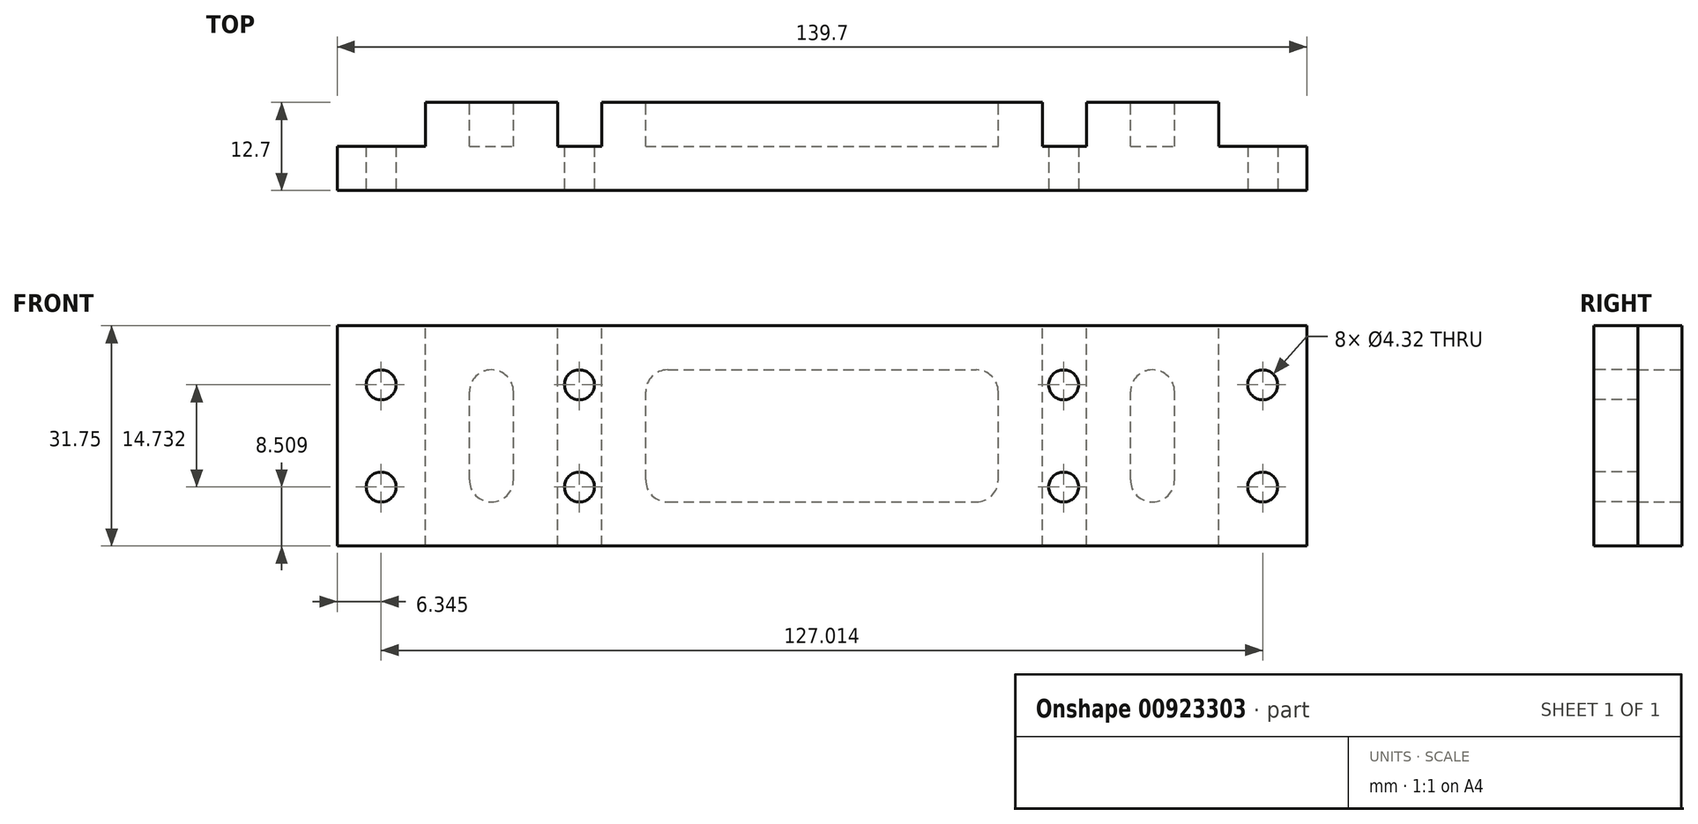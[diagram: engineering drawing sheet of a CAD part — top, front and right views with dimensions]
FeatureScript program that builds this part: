
annotation { "Feature Type Name" : "Feature", "Feature Type Description" : "" }
export const myFeature = defineFeature(function(context is Context, id is Id, definition is map)
    precondition{}
    {
        {
            var Q0;
            Q0=qCreatedBy(makeId("Right.planeOp"),FACE);
            var sketch = newSketch(context, id + "F0", { "sketchPlane" : qUnion([Q0])});
            skLineSegment(sketch, "E0.bottom", {"start": v(0, 0) * mm, "end": v(12.7, 0) * mm});
            skLineSegment(sketch, "E0.top", {"start": v(0, 31.75) * mm, "end": v(12.7, 31.75) * mm});
            skLineSegment(sketch, "E0.left", {"start": v(0, 0) * mm, "end": v(0, 31.75) * mm});
            skLineSegment(sketch, "E0.right", {"start": v(12.7, 0) * mm, "end": v(12.7, 31.75) * mm});
            skSolve(sketch);
        }
        {
            var Q0;
            Q0=makeQuery(id+"F0.imprint","IMPRINT",FACE,{"disambiguationData":[TD([[makeQuery(id+"F0.imprint","IMPRINT",EDGE,{"derivedFrom":sQuery(id+"F0.wireOp",EDGE,"E0.bottom")}),1.0]])]});
            extrude(context, id + "F1", {"entities" : qUnion([Q0]), "depth" : 139.7 * mm, "offsetDistance" : 25.4 * mm});
        }
        {
            var Q0;
            Q0=makeQuery(id+"F1.opExtrude","SWEPT_FACE",FACE,{"disambiguationData":[OSD([sQuery(id+"F0.wireOp",EDGE,"E0.top")])]});
            var sketch = newSketch(context, id + "F2", { "sketchPlane" : qUnion([Q0])});
            skLineSegment(sketch, "E1.bottom", {"start": v(0, 12.7) * mm, "end": v(12.7, 12.7) * mm});
            skLineSegment(sketch, "E1.top", {"start": v(0, 6.35) * mm, "end": v(12.7, 6.35) * mm});
            skLineSegment(sketch, "E1.left", {"start": v(0, 12.7) * mm, "end": v(0, 6.35) * mm});
            skLineSegment(sketch, "E1.right", {"start": v(12.7, 12.7) * mm, "end": v(12.7, 6.35) * mm});
            skLineSegment(sketch, "E2.bottom", {"start": v(139.7, 12.7) * mm, "end": v(127, 12.7) * mm});
            skLineSegment(sketch, "E2.top", {"start": v(139.7, 6.35) * mm, "end": v(127, 6.35) * mm});
            skLineSegment(sketch, "E2.left", {"start": v(139.7, 12.7) * mm, "end": v(139.7, 6.35) * mm});
            skLineSegment(sketch, "E2.right", {"start": v(127, 12.7) * mm, "end": v(127, 6.35) * mm});
            skLineSegment(sketch, "E3.bottom", {"start": v(31.75, 12.7) * mm, "end": v(38.1, 12.7) * mm});
            skLineSegment(sketch, "E3.top", {"start": v(31.75, 6.35) * mm, "end": v(38.1, 6.35) * mm});
            skLineSegment(sketch, "E3.left", {"start": v(31.75, 12.7) * mm, "end": v(31.75, 6.35) * mm});
            skLineSegment(sketch, "E3.right", {"start": v(38.1, 12.7) * mm, "end": v(38.1, 6.35) * mm});
            skLineSegment(sketch, "E4.bottom", {"start": v(101.6, 12.7) * mm, "end": v(107.95, 12.7) * mm});
            skLineSegment(sketch, "E4.top", {"start": v(101.6, 6.35) * mm, "end": v(107.95, 6.35) * mm});
            skLineSegment(sketch, "E4.left", {"start": v(101.6, 12.7) * mm, "end": v(101.6, 6.35) * mm});
            skLineSegment(sketch, "E4.right", {"start": v(107.95, 12.7) * mm, "end": v(107.95, 6.35) * mm});
            skSolve(sketch);
        }
        {
            var Q0;
            Q0=makeQuery(id+"F2.imprint","IMPRINT",FACE,{"disambiguationData":[TD([[makeQuery(id+"F2.imprint","IMPRINT",EDGE,{"derivedFrom":sQuery(id+"F2.wireOp",EDGE,"E1.bottom")}),1.0]])]});
            var Q1;
            Q1=makeQuery(id+"F2.imprint","IMPRINT",FACE,{"disambiguationData":[TD([[makeQuery(id+"F2.imprint","IMPRINT",EDGE,{"derivedFrom":sQuery(id+"F2.wireOp",EDGE,"E3.bottom")}),1.0]])]});
            var Q2;
            Q2=makeQuery(id+"F2.imprint","IMPRINT",FACE,{"disambiguationData":[TD([[makeQuery(id+"F2.imprint","IMPRINT",EDGE,{"derivedFrom":sQuery(id+"F2.wireOp",EDGE,"E4.bottom")}),1.0]])]});
            var Q3;
            Q3=makeQuery(id+"F2.imprint","IMPRINT",FACE,{"disambiguationData":[TD([[makeQuery(id+"F2.imprint","IMPRINT",EDGE,{"derivedFrom":sQuery(id+"F2.wireOp",EDGE,"E2.bottom")}),1.0]])]});
            extrude(context, id + "F3", {"entities" : qUnion([Q0, Q1, Q2, Q3]), "operationType" : NewBodyOperationType.REMOVE, "endBound" : BoundingType.THROUGH_ALL, "oppositeDirection" : true, "depth" : 25.4 * mm, "offsetDistance" : 25.4 * mm});
        }
        {
            var Q0;
            Q0=makeQuery(id+"F1.opExtrude","SWEPT_FACE",FACE,{"disambiguationData":[OSD([sQuery(id+"F0.wireOp",EDGE,"E0.left")])]});
            var sketch = newSketch(context, id + "F4", { "sketchPlane" : qUnion([Q0])});
            skCircle(sketch, "E5", {"center": v(6.34, 23.24) * mm, "radius": 2.16 * mm});
            skCircle(sketch, "E6", {"center": v(6.34, 8.5) * mm, "radius": 2.16 * mm});
            skCircle(sketch, "E7", {"center": v(133.36, 23.24) * mm, "radius": 2.16 * mm});
            skCircle(sketch, "E8", {"center": v(133.36, 8.5) * mm, "radius": 2.16 * mm});
            skLineSegment(sketch, "E9", {"start": v(6.34, 23.24) * mm, "end": v(133.36, 23.24) * mm});
            skLineSegment(sketch, "E10", {"start": v(6.34, 8.5) * mm, "end": v(133.36, 8.5) * mm});
            skSolve(sketch);
        }
        {
            var Q0;
            Q0=makeQuery(id+"F4.imprint","IMPRINT",FACE,{"disambiguationData":[TD([[makeQuery(id+"F4.imprint","IMPRINT",EDGE,{"derivedFrom":sQuery(id+"F4.wireOp",EDGE,"E5")}),1.0]])]});
            var Q1;
            Q1=makeQuery(id+"F4.imprint","IMPRINT",FACE,{"disambiguationData":[TD([[makeQuery(id+"F4.imprint","IMPRINT",EDGE,{"derivedFrom":sQuery(id+"F4.wireOp",EDGE,"E6")}),1.0]])]});
            var Q2;
            Q2=makeQuery(id+"F4.imprint","IMPRINT",FACE,{"disambiguationData":[TD([[makeQuery(id+"F4.imprint","IMPRINT",EDGE,{"derivedFrom":sQuery(id+"F4.wireOp",EDGE,"E8")}),1.0]])]});
            var Q3;
            Q3=makeQuery(id+"F4.imprint","IMPRINT",FACE,{"disambiguationData":[TD([[makeQuery(id+"F4.imprint","IMPRINT",EDGE,{"derivedFrom":sQuery(id+"F4.wireOp",EDGE,"E7")}),1.0]])]});
            var Q4;
            Q4=sQuery(id+"F4.wireOp",EDGE,"E8");
            var Q5;
            Q5=sQuery(id+"F4.wireOp",EDGE,"E7");
            var Q6;
            Q6=sQuery(id+"F4.wireOp",EDGE,"E6");
            var Q7;
            Q7=sQuery(id+"F4.wireOp",EDGE,"E5");
            extrude(context, id + "F5", {"entities" : qUnion([Q0, Q1, Q2, Q3]), "operationType" : NewBodyOperationType.REMOVE, "surfaceEntities" : qUnion([Q4, Q5, Q6, Q7]), "oppositeDirection" : true, "depth" : 25.4 * mm, "offsetDistance" : 25.4 * mm});
        }
        {
            var Q0;
            Q0=makeQuery(id+"F1.opExtrude","SWEPT_FACE",FACE,{"disambiguationData":[OSD([sQuery(id+"F0.wireOp",EDGE,"E0.left")])]});
            var sketch = newSketch(context, id + "F6", { "sketchPlane" : qUnion([Q0])});
            skCircle(sketch, "E11", {"center": v(34.92, 23.24) * mm, "radius": 2.16 * mm});
            skCircle(sketch, "E12", {"center": v(34.92, 8.5) * mm, "radius": 2.16 * mm});
            skCircle(sketch, "E13", {"center": v(104.68, 23.24) * mm, "radius": 2.16 * mm});
            skCircle(sketch, "E14", {"center": v(104.68, 8.5) * mm, "radius": 2.16 * mm});
            skSolve(sketch);
        }
        {
            var Q0;
            Q0=makeQuery(id+"F6.imprint","IMPRINT",FACE,{"disambiguationData":[TD([[makeQuery(id+"F6.imprint","IMPRINT",EDGE,{"derivedFrom":sQuery(id+"F6.wireOp",EDGE,"E11")}),1.0]])]});
            var Q1;
            Q1=makeQuery(id+"F6.imprint","IMPRINT",FACE,{"disambiguationData":[TD([[makeQuery(id+"F6.imprint","IMPRINT",EDGE,{"derivedFrom":sQuery(id+"F6.wireOp",EDGE,"E12")}),1.0]])]});
            var Q2;
            Q2=makeQuery(id+"F6.imprint","IMPRINT",FACE,{"disambiguationData":[TD([[makeQuery(id+"F6.imprint","IMPRINT",EDGE,{"derivedFrom":sQuery(id+"F6.wireOp",EDGE,"E14")}),1.0]])]});
            var Q3;
            Q3=makeQuery(id+"F6.imprint","IMPRINT",FACE,{"disambiguationData":[TD([[makeQuery(id+"F6.imprint","IMPRINT",EDGE,{"derivedFrom":sQuery(id+"F6.wireOp",EDGE,"E13")}),1.0]])]});
            var Q4;
            Q4=sQuery(id+"F6.wireOp",EDGE,"E11");
            var Q5;
            Q5=sQuery(id+"F6.wireOp",EDGE,"E12");
            var Q6;
            Q6=sQuery(id+"F6.wireOp",EDGE,"E14");
            var Q7;
            Q7=sQuery(id+"F6.wireOp",EDGE,"E13");
            extrude(context, id + "F7", {"entities" : qUnion([Q0, Q1, Q2, Q3]), "operationType" : NewBodyOperationType.REMOVE, "surfaceEntities" : qUnion([Q4, Q5, Q6, Q7]), "oppositeDirection" : true, "depth" : 25.4 * mm, "offsetDistance" : 25.4 * mm});
        }
        {
            var Q0;
            Q0=makeQuery(id+"F3.boolean.opBoolean","SPLIT",FACE,{"disambiguationData":[TD([makeQuery(id+"F3.opExtrude","SWEPT_FACE",FACE,{"disambiguationData":[OSD([sQuery(id+"F2.wireOp",EDGE,"E3.right")])]})])],"derivedFrom":makeQuery(id+"F1.opExtrude","SWEPT_FACE",FACE,{"disambiguationData":[OSD([sQuery(id+"F0.wireOp",EDGE,"E0.right")])]})});
            var sketch = newSketch(context, id + "F8", { "sketchPlane" : qUnion([Q0])});
            skLineSegment(sketch, "E15.bottom", {"start": v(-44.45, 6.35) * mm, "end": v(-95.25, 6.35) * mm});
            skLineSegment(sketch, "E15.top", {"start": v(-44.45, 25.4) * mm, "end": v(-95.25, 25.4) * mm});
            skLineSegment(sketch, "E15.left", {"start": v(-44.45, 6.35) * mm, "end": v(-44.45, 25.4) * mm});
            skLineSegment(sketch, "E15.right", {"start": v(-95.25, 6.35) * mm, "end": v(-95.25, 25.4) * mm});
            skSolve(sketch);
        }
        {
            var Q0;
            Q0 = qSketchRegion(id + "F8", true);
            extrude(context, id + "F9", {"entities" : qUnion([Q0]), "operationType" : NewBodyOperationType.REMOVE, "oppositeDirection" : true, "depth" : 6.35 * mm, "offsetDistance" : 25.4 * mm});
        }
        {
            var Q0;
            Q0=makeQuery(id+"F3.boolean.opBoolean","SPLIT",FACE,{"disambiguationData":[TD([makeQuery(id+"F3.opExtrude","SWEPT_FACE",FACE,{"disambiguationData":[OSD([sQuery(id+"F2.wireOp",EDGE,"E1.right")])]})])],"derivedFrom":makeQuery(id+"F1.opExtrude","SWEPT_FACE",FACE,{"disambiguationData":[OSD([sQuery(id+"F0.wireOp",EDGE,"E0.right")])]})});
            var sketch = newSketch(context, id + "F10", { "sketchPlane" : qUnion([Q0])});
            skLineSegment(sketch, "E16.bottom", {"start": v(-19.05, 6.35) * mm, "end": v(-25.4, 6.35) * mm});
            skLineSegment(sketch, "E16.top", {"start": v(-19.05, 25.4) * mm, "end": v(-25.4, 25.4) * mm});
            skLineSegment(sketch, "E16.left", {"start": v(-19.05, 6.35) * mm, "end": v(-19.05, 25.4) * mm});
            skLineSegment(sketch, "E16.right", {"start": v(-25.4, 6.35) * mm, "end": v(-25.4, 25.4) * mm});
            skLineSegment(sketch, "E17.bottom", {"start": v(-114.3, 6.35) * mm, "end": v(-120.65, 6.35) * mm});
            skLineSegment(sketch, "E17.top", {"start": v(-114.3, 25.4) * mm, "end": v(-120.65, 25.4) * mm});
            skLineSegment(sketch, "E17.left", {"start": v(-114.3, 6.35) * mm, "end": v(-114.3, 25.4) * mm});
            skLineSegment(sketch, "E17.right", {"start": v(-120.65, 6.35) * mm, "end": v(-120.65, 25.4) * mm});
            skSolve(sketch);
        }
        {
            var Q0;
            Q0 = qSketchRegion(id + "F10", true);
            extrude(context, id + "F11", {"entities" : qUnion([Q0]), "operationType" : NewBodyOperationType.REMOVE, "oppositeDirection" : true, "depth" : 6.35 * mm, "offsetDistance" : 25.4 * mm});
        }
        {
            var Q0;
            Q0=makeQuery(id+"F11.boolean.opBoolean","COPY",EDGE,{"derivedFrom":makeQuery(id+"F11.opExtrude","SWEPT_EDGE",EDGE,{"disambiguationData":[OSD([sQuery(id+"F10.wireOp",EDGE,"E16.bottom"),sQuery(id+"F10.wireOp",EDGE,"E16.left")])]})});
            var Q1;
            Q1=makeQuery(id+"F11.boolean.opBoolean","COPY",EDGE,{"derivedFrom":makeQuery(id+"F11.opExtrude","SWEPT_EDGE",EDGE,{"disambiguationData":[OSD([sQuery(id+"F10.wireOp",EDGE,"E16.bottom"),sQuery(id+"F10.wireOp",EDGE,"E16.right")])]})});
            var Q2;
            Q2=makeQuery(id+"F11.boolean.opBoolean","COPY",EDGE,{"derivedFrom":makeQuery(id+"F11.opExtrude","SWEPT_EDGE",EDGE,{"disambiguationData":[OSD([sQuery(id+"F10.wireOp",EDGE,"E16.top"),sQuery(id+"F10.wireOp",EDGE,"E16.left")])]})});
            var Q3;
            Q3=makeQuery(id+"F11.boolean.opBoolean","COPY",EDGE,{"derivedFrom":makeQuery(id+"F11.opExtrude","SWEPT_EDGE",EDGE,{"disambiguationData":[OSD([sQuery(id+"F10.wireOp",EDGE,"E16.top"),sQuery(id+"F10.wireOp",EDGE,"E16.right")])]})});
            var Q4;
            Q4=makeQuery(id+"F9.boolean.opBoolean","COPY",EDGE,{"derivedFrom":makeQuery(id+"F9.opExtrude","SWEPT_EDGE",EDGE,{"disambiguationData":[OSD([sQuery(id+"F8.wireOp",EDGE,"E15.bottom"),sQuery(id+"F8.wireOp",EDGE,"E15.left")])]})});
            var Q5;
            Q5=makeQuery(id+"F9.boolean.opBoolean","COPY",EDGE,{"derivedFrom":makeQuery(id+"F9.opExtrude","SWEPT_EDGE",EDGE,{"disambiguationData":[OSD([sQuery(id+"F8.wireOp",EDGE,"E15.bottom"),sQuery(id+"F8.wireOp",EDGE,"E15.right")])]})});
            var Q6;
            Q6=makeQuery(id+"F9.boolean.opBoolean","COPY",EDGE,{"derivedFrom":makeQuery(id+"F9.opExtrude","SWEPT_EDGE",EDGE,{"disambiguationData":[OSD([sQuery(id+"F8.wireOp",EDGE,"E15.top"),sQuery(id+"F8.wireOp",EDGE,"E15.right")])]})});
            var Q7;
            Q7=makeQuery(id+"F9.boolean.opBoolean","COPY",EDGE,{"derivedFrom":makeQuery(id+"F9.opExtrude","SWEPT_EDGE",EDGE,{"disambiguationData":[OSD([sQuery(id+"F8.wireOp",EDGE,"E15.top"),sQuery(id+"F8.wireOp",EDGE,"E15.left")])]})});
            var Q8;
            Q8=makeQuery(id+"F11.boolean.opBoolean","COPY",EDGE,{"derivedFrom":makeQuery(id+"F11.opExtrude","SWEPT_EDGE",EDGE,{"disambiguationData":[OSD([sQuery(id+"F10.wireOp",EDGE,"E17.bottom"),sQuery(id+"F10.wireOp",EDGE,"E17.right")])]})});
            var Q9;
            Q9=makeQuery(id+"F11.boolean.opBoolean","COPY",EDGE,{"derivedFrom":makeQuery(id+"F11.opExtrude","SWEPT_EDGE",EDGE,{"disambiguationData":[OSD([sQuery(id+"F10.wireOp",EDGE,"E17.top"),sQuery(id+"F10.wireOp",EDGE,"E17.right")])]})});
            var Q10;
            Q10=makeQuery(id+"F11.boolean.opBoolean","COPY",EDGE,{"derivedFrom":makeQuery(id+"F11.opExtrude","SWEPT_EDGE",EDGE,{"disambiguationData":[OSD([sQuery(id+"F10.wireOp",EDGE,"E17.top"),sQuery(id+"F10.wireOp",EDGE,"E17.left")])]})});
            var Q11;
            Q11=makeQuery(id+"F11.boolean.opBoolean","COPY",EDGE,{"derivedFrom":makeQuery(id+"F11.opExtrude","SWEPT_EDGE",EDGE,{"disambiguationData":[OSD([sQuery(id+"F10.wireOp",EDGE,"E17.bottom"),sQuery(id+"F10.wireOp",EDGE,"E17.left")])]})});
            fillet(context, id + "F12", {"entities" : qUnion([Q0, Q1, Q2, Q3, Q4, Q5, Q6, Q7, Q8, Q9, Q10, Q11]), "radius" : 3.17 * mm, "tangentPropagation" : true, "allowEdgeOverflow" : false});
        }
    });
